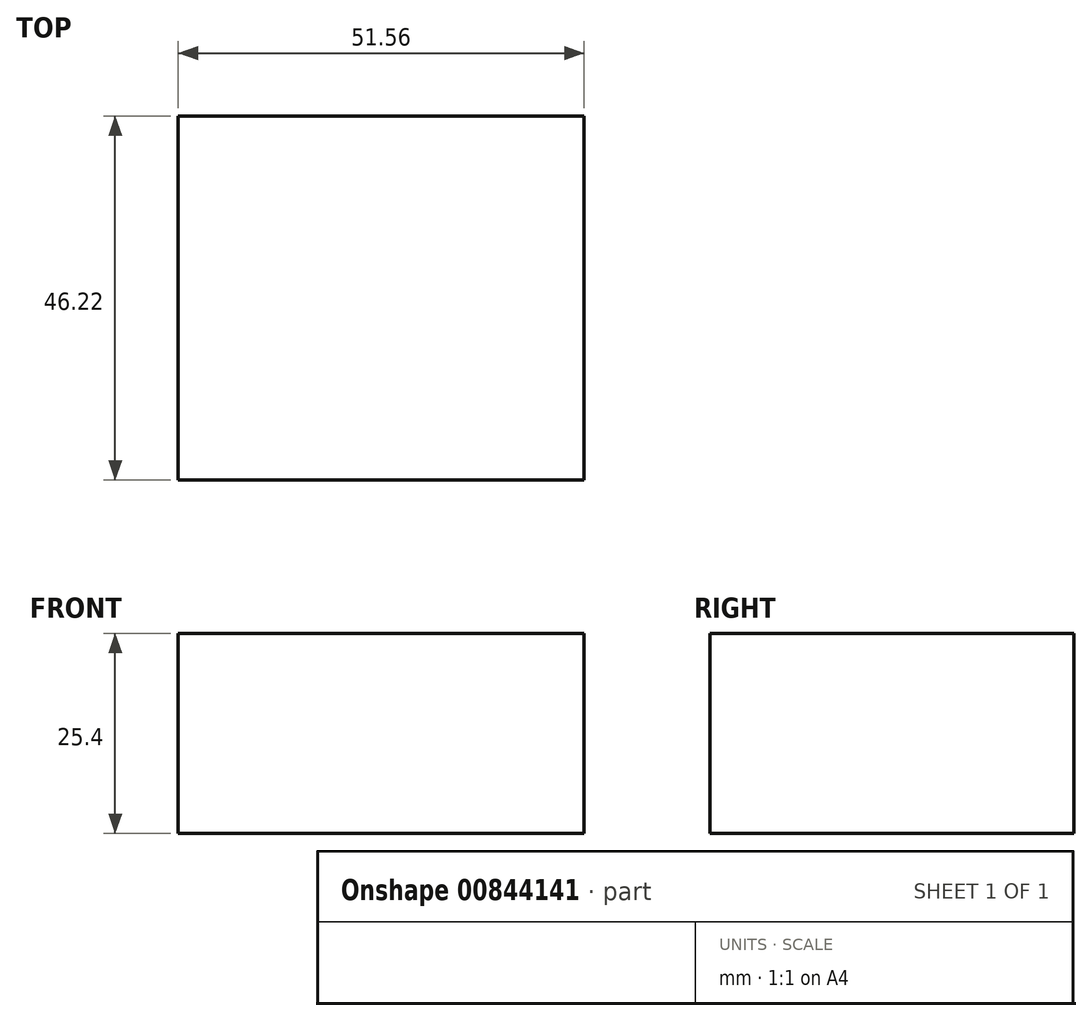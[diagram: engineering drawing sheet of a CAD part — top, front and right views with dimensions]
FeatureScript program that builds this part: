
annotation { "Feature Type Name" : "Feature", "Feature Type Description" : "" }
export const myFeature = defineFeature(function(context is Context, id is Id, definition is map)
    precondition{}
    {
        {
            var Q0;
            Q0=qCreatedBy(makeId("Top.planeOp"),FACE);
            var sketch = newSketch(context, id + "F0", { "sketchPlane" : qUnion([Q0])});
            skLineSegment(sketch, "E0.bottom", {"start": v(-26.52, 22.37) * mm, "end": v(25.04, 22.37) * mm});
            skLineSegment(sketch, "E0.top", {"start": v(-26.52, -23.85) * mm, "end": v(25.04, -23.85) * mm});
            skLineSegment(sketch, "E0.left", {"start": v(-26.52, 22.37) * mm, "end": v(-26.52, -23.85) * mm});
            skLineSegment(sketch, "E0.right", {"start": v(25.04, 22.37) * mm, "end": v(25.04, -23.85) * mm});
            skSolve(sketch);
        }
        {
            var Q0;
            Q0=makeQuery(id+"F0.imprint","IMPRINT",FACE,{"disambiguationData":[TD([[makeQuery(id+"F0.imprint","IMPRINT",EDGE,{"derivedFrom":sQuery(id+"F0.wireOp",EDGE,"E0.bottom")}),-1.0]])]});
            extrude(context, id + "F1", {"entities" : qUnion([Q0]), "depth" : 25.4 * mm, "offsetDistance" : 25.4 * mm});
        }
    });
